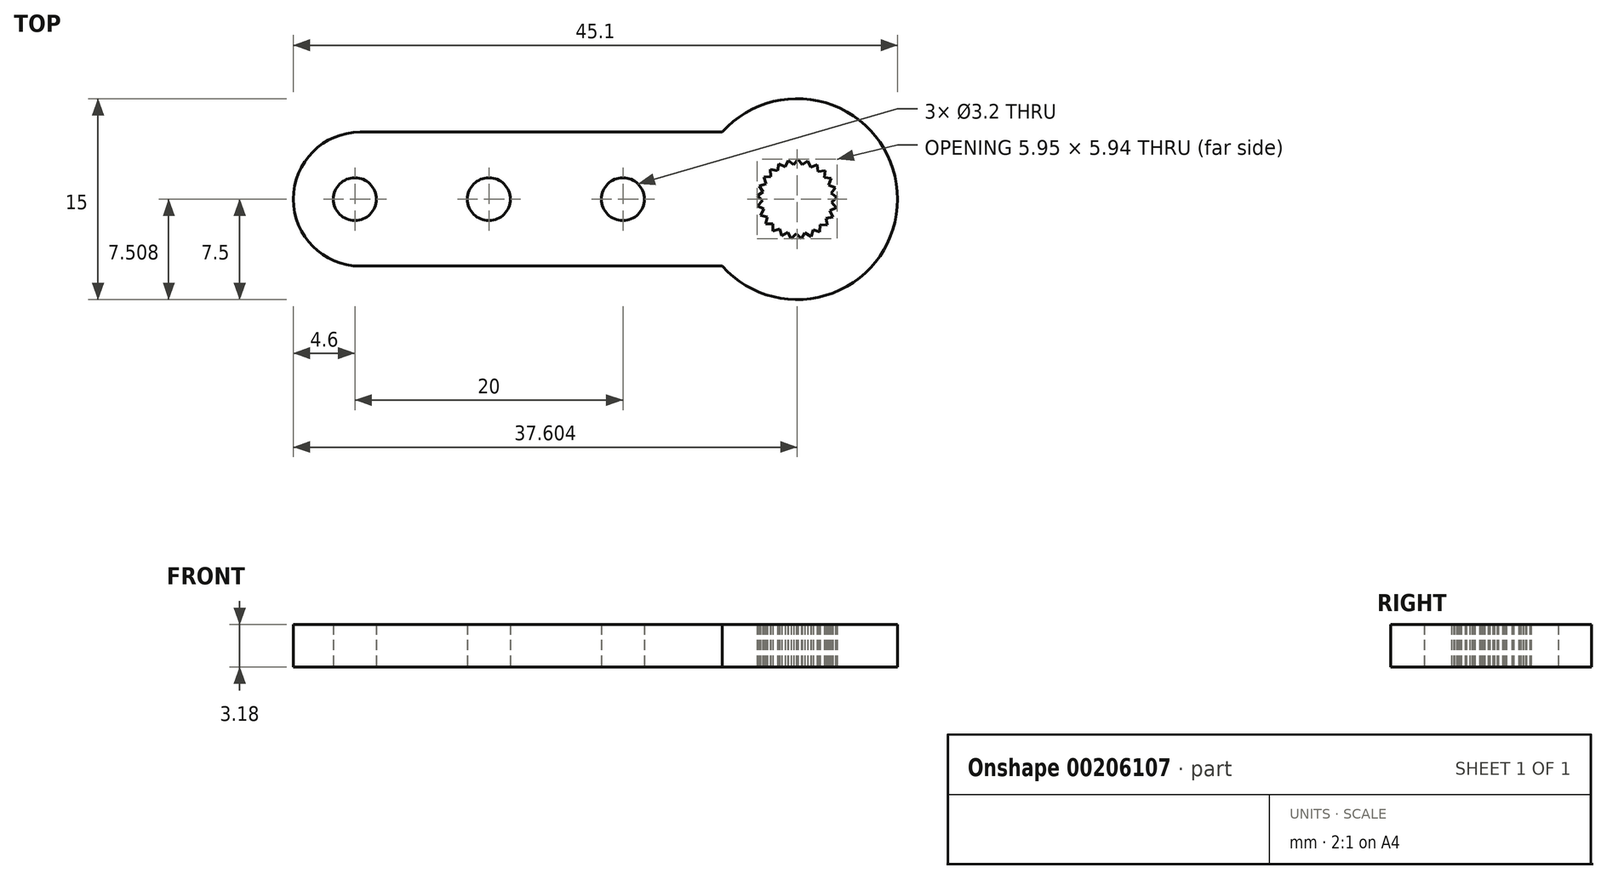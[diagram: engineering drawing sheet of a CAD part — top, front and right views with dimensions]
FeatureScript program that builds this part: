
annotation { "Feature Type Name" : "Feature", "Feature Type Description" : "" }
export const myFeature = defineFeature(function(context is Context, id is Id, definition is map)
    precondition{}
    {
        {
            var Q0;
            Q0=qCreatedBy(makeId("Top.planeOp"),FACE);
            var sketch = newSketch(context, id + "F0", { "sketchPlane" : qUnion([Q0])});
            skLineSegment(sketch, "E0.bottom", {"start": v(-5.6, 5) * mm, "end": v(-32.6, 5) * mm});
            skLineSegment(sketch, "E0.top", {"start": v(-5.6, -5) * mm, "end": v(-32.6, -5) * mm});
            skCircle(sketch, "E1", {"center": v(-33, 0) * mm, "radius": 1.6 * mm});
            skCircle(sketch, "E2.1.0.0", {"center": v(-23, 0) * mm, "radius": 1.6 * mm});
            skCircle(sketch, "E2.2.0.0", {"center": v(-13, 0) * mm, "radius": 1.6 * mm});
            skLineSegment(sketch, "E2.direction1", {"start": v(-33, 0) * mm, "end": v(-23, 0) * mm, "construction": true});
            skArc(sketch, "E3", {"start": v(-32.6, 5) * mm, "mid": v(-36.14, 3.54) * mm, "end": v(-37.6, 0) * mm});
            skArc(sketch, "E4.MirrorCS", {"start": v(-32.6, -5) * mm, "mid": v(-36.14, -3.54) * mm, "end": v(-37.6, 0) * mm});
            skLineSegment(sketch, "E5", {"start": v(-2.48, 1.65) * mm, "end": v(-2.31, 1.15) * mm});
            skLineSegment(sketch, "E6", {"start": v(-2.31, 1.15) * mm, "end": v(-2.81, 0.98) * mm});
            skLineSegment(sketch, "E7.1.0", {"start": v(-2.81, 0.98) * mm, "end": v(-2.53, 0.54) * mm});
            skLineSegment(sketch, "E7.1.1", {"start": v(-2.53, 0.54) * mm, "end": v(-2.97, 0.25) * mm});
            skLineSegment(sketch, "E7.2.0", {"start": v(-2.97, 0.25) * mm, "end": v(-2.58, -0.1) * mm});
            skLineSegment(sketch, "E7.2.1", {"start": v(-2.58, -0.1) * mm, "end": v(-2.94, -0.5) * mm});
            skLineSegment(sketch, "E7.3.0", {"start": v(-2.94, -0.5) * mm, "end": v(-2.47, -0.74) * mm});
            skLineSegment(sketch, "E7.3.1", {"start": v(-2.47, -0.74) * mm, "end": v(-2.72, -1.2) * mm});
            skLineSegment(sketch, "E7.4.0", {"start": v(-2.72, -1.2) * mm, "end": v(-2.21, -1.34) * mm});
            skLineSegment(sketch, "E7.4.1", {"start": v(-2.21, -1.34) * mm, "end": v(-2.34, -1.85) * mm});
            skLineSegment(sketch, "E7.5.0", {"start": v(-2.34, -1.85) * mm, "end": v(-1.8, -1.84) * mm});
            skLineSegment(sketch, "E7.5.1", {"start": v(-1.8, -1.84) * mm, "end": v(-1.8, -2.37) * mm});
            skLineSegment(sketch, "E7.6.0", {"start": v(-1.8, -2.37) * mm, "end": v(-1.3, -2.24) * mm});
            skLineSegment(sketch, "E7.6.1", {"start": v(-1.3, -2.24) * mm, "end": v(-1.16, -2.75) * mm});
            skLineSegment(sketch, "E7.7.0", {"start": v(-1.16, -2.75) * mm, "end": v(-0.7, -2.49) * mm});
            skLineSegment(sketch, "E7.7.1", {"start": v(-0.7, -2.49) * mm, "end": v(-0.44, -2.95) * mm});
            skLineSegment(sketch, "E7.8.0", {"start": v(-0.44, -2.95) * mm, "end": v(-0.06, -2.58) * mm});
            skLineSegment(sketch, "E7.8.1", {"start": v(-0.06, -2.58) * mm, "end": v(0.3, -2.96) * mm});
            skLineSegment(sketch, "E7.9.0", {"start": v(0.3, -2.96) * mm, "end": v(0.59, -2.52) * mm});
            skLineSegment(sketch, "E7.9.1", {"start": v(0.59, -2.52) * mm, "end": v(1.04, -2.8) * mm});
            skLineSegment(sketch, "E7.10.0", {"start": v(1.04, -2.8) * mm, "end": v(1.2, -2.3) * mm});
            skLineSegment(sketch, "E7.10.1", {"start": v(1.2, -2.3) * mm, "end": v(1.7, -2.45) * mm});
            skLineSegment(sketch, "E7.11.0", {"start": v(1.7, -2.45) * mm, "end": v(1.73, -1.92) * mm});
            skLineSegment(sketch, "E7.11.1", {"start": v(1.73, -1.92) * mm, "end": v(2.25, -1.95) * mm});
            skLineSegment(sketch, "E7.12.0", {"start": v(2.25, -1.95) * mm, "end": v(2.15, -1.43) * mm});
            skLineSegment(sketch, "E7.12.1", {"start": v(2.15, -1.43) * mm, "end": v(2.67, -1.33) * mm});
            skLineSegment(sketch, "E7.13.0", {"start": v(2.67, -1.33) * mm, "end": v(2.44, -0.85) * mm});
            skLineSegment(sketch, "E7.13.1", {"start": v(2.44, -0.85) * mm, "end": v(2.91, -0.62) * mm});
            skLineSegment(sketch, "E7.14.0", {"start": v(2.91, -0.62) * mm, "end": v(2.57, -0.22) * mm});
            skLineSegment(sketch, "E7.14.1", {"start": v(2.57, -0.22) * mm, "end": v(2.98, 0.12) * mm});
            skLineSegment(sketch, "E7.15.0", {"start": v(2.98, 0.12) * mm, "end": v(2.55, 0.43) * mm});
            skLineSegment(sketch, "E7.15.1", {"start": v(2.55, 0.43) * mm, "end": v(2.85, 0.86) * mm});
            skLineSegment(sketch, "E7.16.0", {"start": v(2.85, 0.86) * mm, "end": v(2.36, 1.05) * mm});
            skLineSegment(sketch, "E7.16.1", {"start": v(2.36, 1.05) * mm, "end": v(2.55, 1.54) * mm});
            skLineSegment(sketch, "E7.17.0", {"start": v(2.55, 1.54) * mm, "end": v(2.03, 1.6) * mm});
            skLineSegment(sketch, "E7.17.1", {"start": v(2.03, 1.6) * mm, "end": v(2.09, 2.13) * mm});
            skLineSegment(sketch, "E7.18.0", {"start": v(2.09, 2.13) * mm, "end": v(1.56, 2.06) * mm});
            skLineSegment(sketch, "E7.18.1", {"start": v(1.56, 2.06) * mm, "end": v(1.5, 2.58) * mm});
            skLineSegment(sketch, "E7.19.0", {"start": v(1.5, 2.58) * mm, "end": v(1, 2.38) * mm});
            skLineSegment(sketch, "E7.19.1", {"start": v(1, 2.38) * mm, "end": v(0.8, 2.87) * mm});
            skLineSegment(sketch, "E7.20.0", {"start": v(0.8, 2.87) * mm, "end": v(0.38, 2.56) * mm});
            skLineSegment(sketch, "E7.20.1", {"start": v(0.38, 2.56) * mm, "end": v(0.07, 2.98) * mm});
            skLineSegment(sketch, "E7.21.0", {"start": v(0.07, 2.98) * mm, "end": v(-0.27, 2.57) * mm});
            skLineSegment(sketch, "E7.21.1", {"start": v(-0.27, 2.57) * mm, "end": v(-0.68, 2.9) * mm});
            skLineSegment(sketch, "E7.22.0", {"start": v(-0.68, 2.9) * mm, "end": v(-0.9, 2.42) * mm});
            skLineSegment(sketch, "E7.22.1", {"start": v(-0.9, 2.42) * mm, "end": v(-1.38, 2.64) * mm});
            skLineSegment(sketch, "E7.23.0", {"start": v(-1.38, 2.64) * mm, "end": v(-1.47, 2.12) * mm});
            skLineSegment(sketch, "E7.23.1", {"start": v(-1.47, 2.12) * mm, "end": v(-2, 2.22) * mm});
            skLineSegment(sketch, "E7.24.0", {"start": v(-2, 2.22) * mm, "end": v(-1.95, 1.69) * mm});
            skLineSegment(sketch, "E7.24.1", {"start": v(-1.95, 1.69) * mm, "end": v(-2.48, 1.65) * mm});
            skPoint(sketch, "E7.center", {"position": v(0, 0) * mm});
            skArc(sketch, "E8", {"start": v(-5.6, -5) * mm, "mid": v(2.68, -7) * mm, "end": v(7.5, 0) * mm});
            skPoint(sketch, "E9.orphan", {"position": v(0, 5) * mm});
            skPoint(sketch, "E10.orphan", {"position": v(0, -5) * mm});
            skArc(sketch, "E11.trimOffspring", {"start": v(7.5, 0) * mm, "mid": v(2.68, 7) * mm, "end": v(-5.6, 5) * mm});
            skLineSegment(sketch, "E12", {"start": v(7.5, 0) * mm, "end": v(7.5, 0) * mm});
            skSolve(sketch);
        }
        {
            var Q0;
            Q0=makeQuery(id+"F0.imprint","IMPRINT",FACE,{"disambiguationData":[TD([[makeQuery(id+"F0.imprint","IMPRINT",EDGE,{"derivedFrom":sQuery(id+"F0.wireOp",EDGE,"E2.2.0.0")}),-1.0]])]});
            extrude(context, id + "F1", {"entities" : qUnion([Q0]), "depth" : 3.17 * mm});
        }
    });
